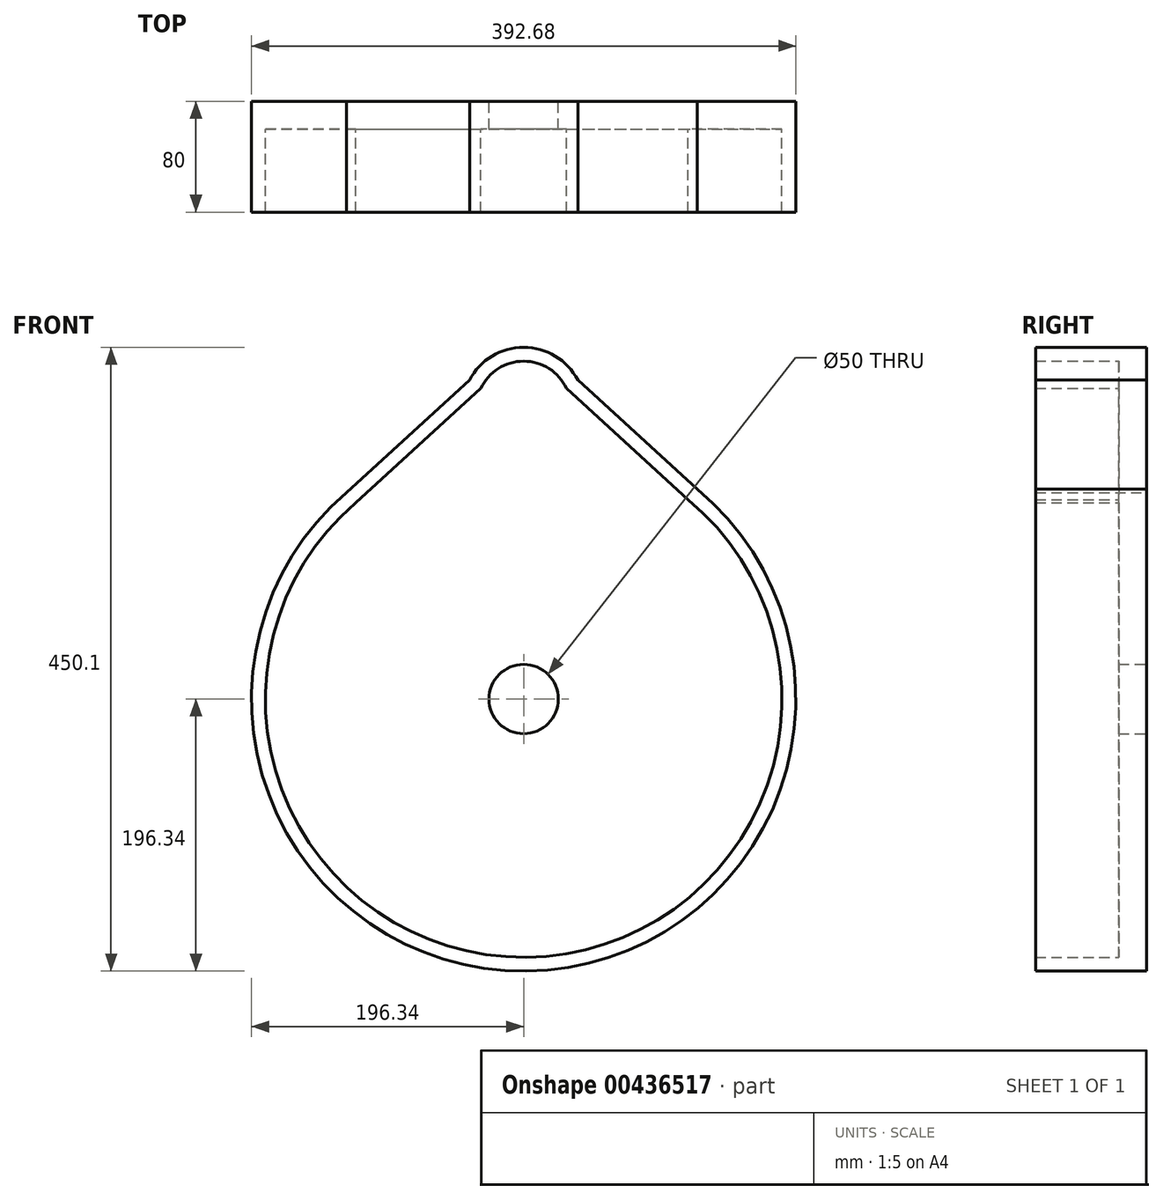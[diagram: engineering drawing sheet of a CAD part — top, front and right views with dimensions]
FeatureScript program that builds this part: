
annotation { "Feature Type Name" : "Feature", "Feature Type Description" : "" }
export const myFeature = defineFeature(function(context is Context, id is Id, definition is map)
    precondition{}
    {
        {
            var Q0;
            Q0=qCreatedBy(makeId("Front.planeOp"),FACE);
            var sketch = newSketch(context, id + "F0", { "sketchPlane" : qUnion([Q0])});
            skLineSegment(sketch, "E0", {"start": v(0, 0) * mm, "end": v(0, 200) * mm, "construction": true});
            skArc(sketch, "E1", {"start": v(-127.9, 148.97) * mm, "mid": v(1.84, -196.33) * mm, "end": v(125.07, 151.34) * mm});
            skLineSegment(sketch, "E2", {"start": v(-127.9, 148.97) * mm, "end": v(-39.04, 230.16) * mm});
            skLineSegment(sketch, "E3", {"start": v(39.04, 230.16) * mm, "end": v(125.07, 151.34) * mm});
            skArc(sketch, "E4.trimOffspring", {"start": v(39.04, 230.16) * mm, "mid": v(0, 253.76) * mm, "end": v(-39.04, 230.16) * mm});
            skLineSegment(sketch, "E5.0", {"start": v(-121.26, 141.48) * mm, "end": v(-30.92, 224.04) * mm});
            skArc(sketch, "E5.1", {"start": v(-121.26, 141.48) * mm, "mid": v(1.8, -186.33) * mm, "end": v(118.5, 143.8) * mm});
            skLineSegment(sketch, "E5.2", {"start": v(30.91, 224.05) * mm, "end": v(118.5, 143.8) * mm});
            skArc(sketch, "E5.3", {"start": v(30.91, 224.05) * mm, "mid": v(0, 243.76) * mm, "end": v(-30.92, 224.04) * mm});
            skCircle(sketch, "E6", {"center": v(0, 0) * mm, "radius": 25 * mm});
            skSolve(sketch);
        }
        {
            var Q0;
            Q0=makeQuery(id+"F0.imprint","IMPRINT",FACE,{"disambiguationData":[TD([[makeQuery(id+"F0.imprint","IMPRINT",EDGE,{"derivedFrom":sQuery(id+"F0.wireOp",EDGE,"E1")}),1.0]])]});
            var Q1;
            Q1=makeQuery(id+"F0.imprint","IMPRINT",FACE,{"disambiguationData":[TD([[makeQuery(id+"F0.imprint","IMPRINT",EDGE,{"derivedFrom":sQuery(id+"F0.wireOp",EDGE,"E5.0")}),-1.0]])]});
            extrude(context, id + "F1", {"entities" : qUnion([Q0, Q1]), "depth" : 20 * mm});
        }
        {
            var Q0;
            Q0=makeQuery(id+"F0.imprint","IMPRINT",FACE,{"disambiguationData":[TD([[makeQuery(id+"F0.imprint","IMPRINT",EDGE,{"derivedFrom":sQuery(id+"F0.wireOp",EDGE,"E1")}),1.0]])]});
            extrude(context, id + "F2", {"entities" : qUnion([Q0]), "operationType" : NewBodyOperationType.ADD, "depth" : 80 * mm, "hasSecondDirection" : true, "secondDirectionOppositeDirection" : false, "secondDirectionDepth" : 20 * mm});
        }
    });
